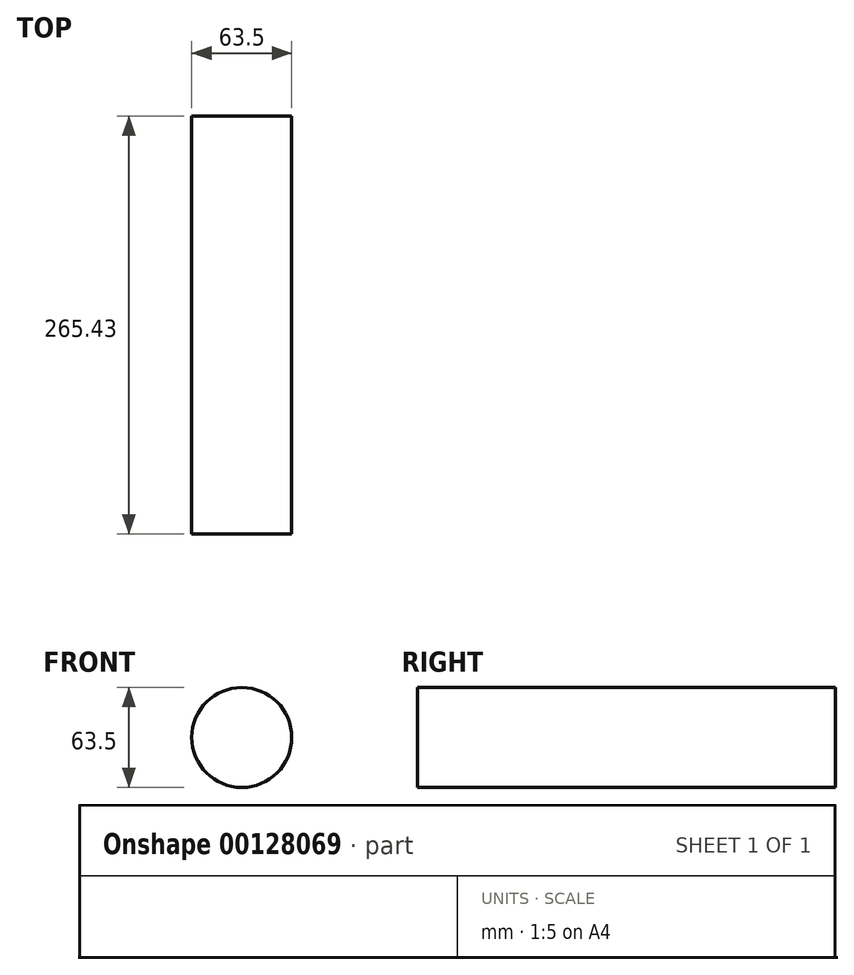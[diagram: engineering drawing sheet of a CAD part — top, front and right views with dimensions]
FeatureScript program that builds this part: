
annotation { "Feature Type Name" : "Feature", "Feature Type Description" : "" }
export const myFeature = defineFeature(function(context is Context, id is Id, definition is map)
    precondition{}
    {
        {
            var Q0;
            Q0=qCreatedBy(makeId("Front.planeOp"),FACE);
            var sketch = newSketch(context, id + "F0", { "sketchPlane" : qUnion([Q0])});
            skCircle(sketch, "E0", {"center": v(0, 0) * mm, "radius": 31.75 * mm});
            skSolve(sketch);
        }
        {
            var Q0;
            Q0=makeQuery(id+"F0.imprint","IMPRINT",FACE,{"disambiguationData":[TD([[makeQuery(id+"F0.imprint","IMPRINT",EDGE,{"derivedFrom":sQuery(id+"F0.wireOp",EDGE,"E0")}),1.0]])]});
            extrude(context, id + "F1", {"entities" : qUnion([Q0]), "depth" : 265.43 * mm});
        }
    });
